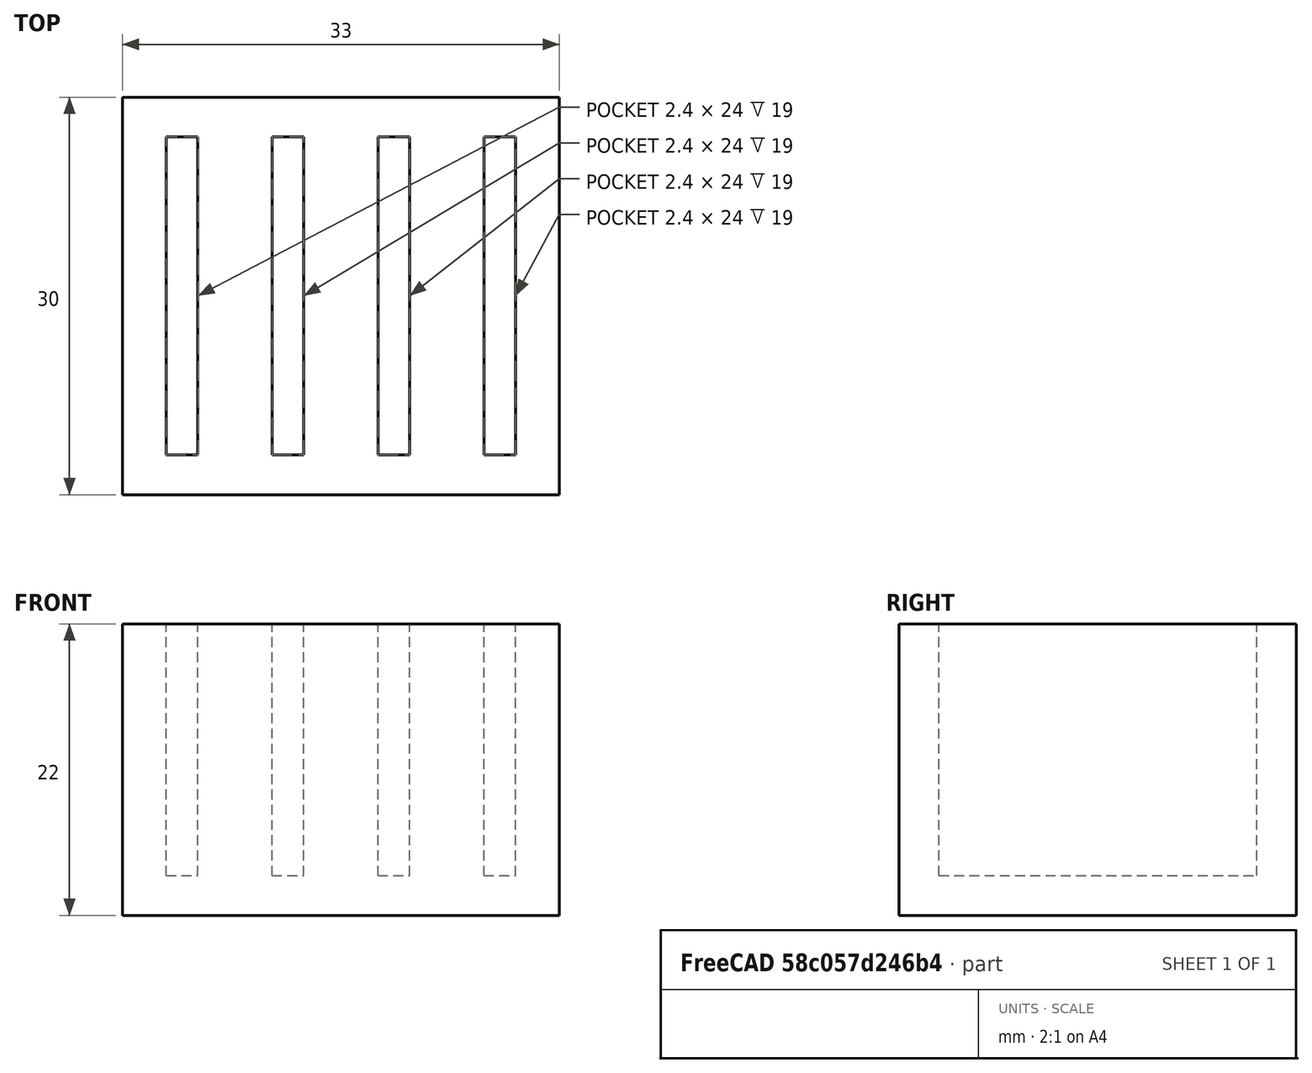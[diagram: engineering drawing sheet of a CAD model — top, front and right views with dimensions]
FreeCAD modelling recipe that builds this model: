
FCSTD DOCUMENT  (FreeCAD 1.0R39319 (Git))
Label: ojt1_t08r01_sd_holder
License: All rights reserved
LicenseURL: https://en.wikipedia.org/wiki/All_rights_reserved
objects: Part::Box×5, Part::MultiFuse×1, Part::Cut×1
note: 7 computed .brp shape members not serialized (recipe doc carries the construction recipe); baked Part::Feature solids carry a one-line shape summary decoded from their .brp

FEATURE [Part::Box] Box  label="Cub"
  AttacherType = Attacher::AttachEngine3D
  Height = 22
  Length = 2.4
  Placement = pos=(3.3,3,3) rot=(0,0,1;0rad)
  Width = 24
FEATURE [Part::Box] Box001  label="Cub001"
  AttacherType = Attacher::AttachEngine3D
  Height = 22
  Length = 2.4
  Placement = pos=(11.3,3,3) rot=(0,0,1;0rad)
  Width = 24
FEATURE [Part::Box] Box002  label="Cub002"
  AttacherType = Attacher::AttachEngine3D
  Height = 22
  Length = 2.4
  Placement = pos=(19.3,3,3) rot=(0,0,1;0rad)
  Width = 24
FEATURE [Part::Box] Box003  label="Cub003"
  AttacherType = Attacher::AttachEngine3D
  Height = 22
  Length = 2.4
  Placement = pos=(27.3,3,3) rot=(0,0,1;0rad)
  Width = 24
FEATURE [Part::Box] Box004  label="base"
  AttacherType = Attacher::AttachEngine3D
  Height = 22
  Length = 33
  Width = 30
FEATURE [Part::MultiFuse] Fusion  label="renuras"
  Refine = true
  Shapes = -> [Box,Box001,Box002,Box003]
FEATURE [Part::Cut] Cut
  Base = -> Box004
  Refine = true
  Tool = -> Fusion
